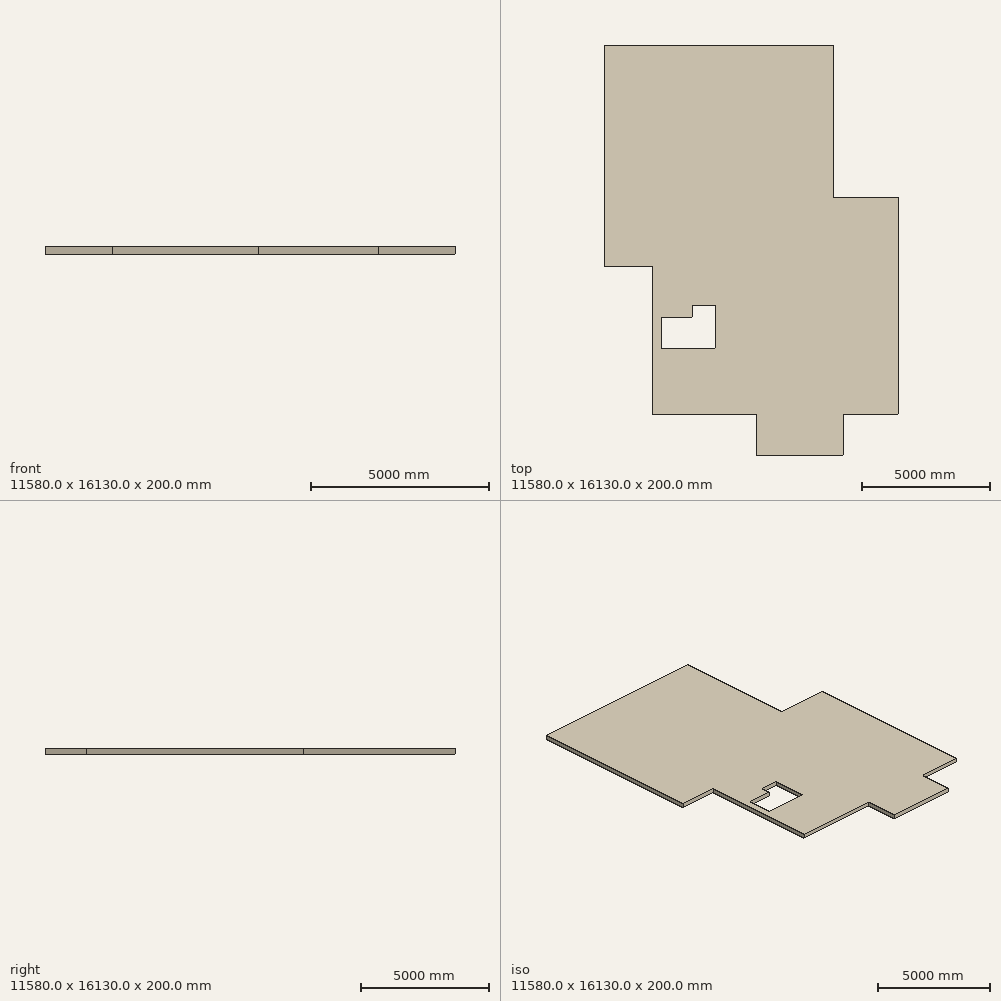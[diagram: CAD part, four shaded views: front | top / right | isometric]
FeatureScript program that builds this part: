
annotation { "Feature Type Name" : "Feature", "Feature Type Description" : "" }
export const myFeature = defineFeature(function(context is Context, id is Id, definition is map)
    precondition{}
    {
        {
            var Q0;
            Q0=qCreatedBy(makeId("Top.planeOp"),FACE);
            var sketch = newSketch(context, id + "F0", { "sketchPlane" : qUnion([Q0])});
            skLineSegment(sketch, "E0.bottom", {"start": v(-5877.53, 9555.7) * mm, "end": v(3122.47, 9555.7) * mm});
            skLineSegment(sketch, "E0.top", {"start": v(-3977.53, -4944.3) * mm, "end": v(127.47, -4944.3) * mm});
            skLineSegment(sketch, "E0.left", {"start": v(-5877.53, 9555.7) * mm, "end": v(-5877.53, 855.7) * mm});
            skLineSegment(sketch, "E1.top", {"start": v(5702.47, 3555.7) * mm, "end": v(3122.47, 3555.7) * mm});
            skLineSegment(sketch, "E1.right", {"start": v(3122.47, 9555.7) * mm, "end": v(3122.47, 3555.7) * mm});
            skLineSegment(sketch, "E2.top", {"start": v(-5877.53, 855.7) * mm, "end": v(-3977.53, 855.7) * mm});
            skLineSegment(sketch, "E3.0", {"start": v(-3977.53, -4944.3) * mm, "end": v(-3977.53, 855.7) * mm});
            skPoint(sketch, "E4.endSnap0", {"position": v(-380.03, 955.7) * mm});
            skPoint(sketch, "E5.orphan", {"position": v(1222.47, 955.7) * mm});
            skPoint(sketch, "E6.orphan", {"position": v(-282.53, 955.7) * mm});
            skPoint(sketch, "E7.trimOffspring.end.orphan", {"position": v(-2177.53, 855.7) * mm});
            skLineSegment(sketch, "E8.0", {"start": v(127.47, -4944.3) * mm, "end": v(127.47, -6574.3) * mm});
            skLineSegment(sketch, "E9.0", {"start": v(3537.47, -6574.3) * mm, "end": v(3537.47, -4944.3) * mm});
            skLineSegment(sketch, "E10.0", {"start": v(127.47, -6574.3) * mm, "end": v(3537.47, -6574.3) * mm});
            skPoint(sketch, "E11.trimOffspring.end.orphan", {"position": v(-1982.53, 955.7) * mm});
            skPoint(sketch, "E12.orphan", {"position": v(-2177.53, 3555.7) * mm});
            skPoint(sketch, "E13.end.orphan", {"position": v(5622.47, -4744.3) * mm});
            skLineSegment(sketch, "E14.0", {"start": v(5702.47, 3555.7) * mm, "end": v(5702.47, -4944.3) * mm});
            skPoint(sketch, "E15.trimOffspring.end.orphan", {"position": v(5622.47, -4944.3) * mm});
            skPoint(sketch, "E16.0.end.orphan", {"position": v(-877.53, 3555.7) * mm});
            skPoint(sketch, "E17.orphan", {"position": v(127.47, -5944.3) * mm});
            skPoint(sketch, "E18.0.end.orphan", {"position": v(942.47, -6574.3) * mm});
            skPoint(sketch, "E19.orphan", {"position": v(-1977.53, 3355.7) * mm});
            skPoint(sketch, "E20.0.start.orphan", {"position": v(-1857.53, 3355.7) * mm});
            skPoint(sketch, "E21.orphan", {"position": v(-537.53, 3555.7) * mm});
            skPoint(sketch, "E22.0.end.orphan", {"position": v(3537.47, -5904.3) * mm});
            skLineSegment(sketch, "E23.trimOffspring", {"start": v(3537.47, -4944.3) * mm, "end": v(5702.47, -4944.3) * mm});
            skSolve(sketch);
        }
        {
            var Q0;
            Q0=makeQuery(id+"F0.imprint","IMPRINT",FACE,{"disambiguationData":[TD([[makeQuery(id+"F0.imprint","IMPRINT",EDGE,{"derivedFrom":sQuery(id+"F0.wireOp",EDGE,"E0.bottom")}),-1.0]])]});
            extrude(context, id + "F1", {"entities" : qUnion([Q0]), "oppositeDirection" : true, "depth" : 200 * mm});
        }
        {
            var Q0;
            Q0=makeQuery(id+"F1.opExtrude","CAP_FACE",FACE,{"disambiguationData":[OSD([sQuery(id+"F0.wireOp",EDGE,"E0.bottom"),sQuery(id+"F0.wireOp",EDGE,"E0.top"),sQuery(id+"F0.wireOp",EDGE,"E0.left"),sQuery(id+"F0.wireOp",EDGE,"E1.top"),sQuery(id+"F0.wireOp",EDGE,"E1.right"),sQuery(id+"F0.wireOp",EDGE,"E2.top"),sQuery(id+"F0.wireOp",EDGE,"E3.0"),sQuery(id+"F0.wireOp",EDGE,"E8.0"),sQuery(id+"F0.wireOp",EDGE,"E9.0"),sQuery(id+"F0.wireOp",EDGE,"E10.0"),sQuery(id+"F0.wireOp",EDGE,"E14.0"),sQuery(id+"F0.wireOp",EDGE,"E23.trimOffspring")])],"isStart":true});
            var sketch = newSketch(context, id + "F2", { "sketchPlane" : qUnion([Q0])});
            skLineSegment(sketch, "E24.0", {"start": v(-3637.53, -2364.3) * mm, "end": v(-1517.53, -2364.3) * mm});
            skLineSegment(sketch, "E25.0", {"start": v(-2417.53, -684.3) * mm, "end": v(-1517.53, -684.3) * mm});
            skLineSegment(sketch, "E26.0", {"start": v(-3637.53, -1144.3) * mm, "end": v(-2417.53, -1144.3) * mm});
            skLineSegment(sketch, "E27.0", {"start": v(-1517.53, -2364.3) * mm, "end": v(-1517.53, -684.3) * mm});
            skLineSegment(sketch, "E28.0", {"start": v(-2417.53, -1144.3) * mm, "end": v(-2417.53, -684.3) * mm});
            skLineSegment(sketch, "E29.0", {"start": v(-3637.53, -2364.3) * mm, "end": v(-3637.53, -1144.3) * mm});
            skSolve(sketch);
        }
        {
            var Q0;
            Q0=makeQuery(id+"F2.imprint","IMPRINT",FACE,{"disambiguationData":[TD([[makeQuery(id+"F2.imprint","IMPRINT",EDGE,{"derivedFrom":sQuery(id+"F2.wireOp",EDGE,"E24.0")}),1.0]])]});
            extrude(context, id + "F3", {"entities" : qUnion([Q0]), "operationType" : NewBodyOperationType.REMOVE, "endBound" : BoundingType.UP_TO_NEXT, "oppositeDirection" : true, "depth" : 25 * mm});
        }
    });
